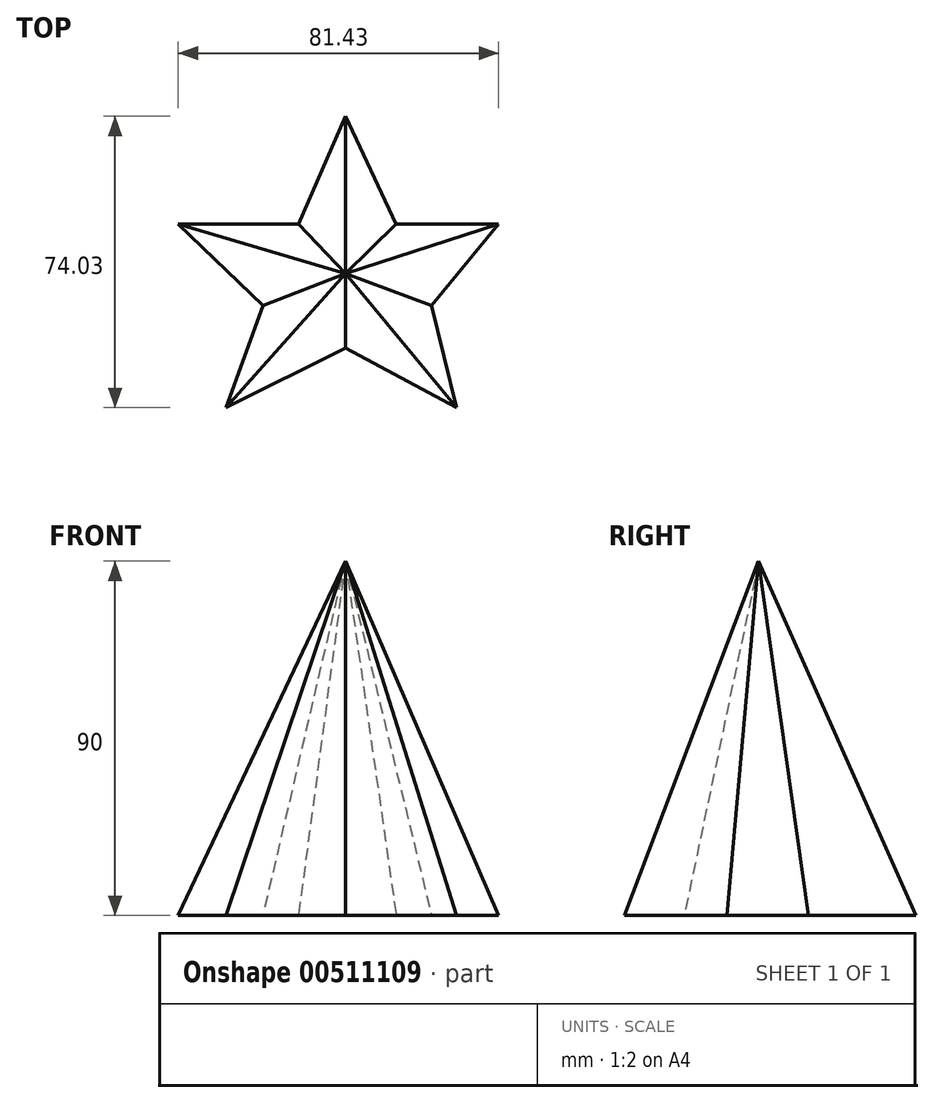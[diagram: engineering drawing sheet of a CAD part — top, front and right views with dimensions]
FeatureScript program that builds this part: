
annotation { "Feature Type Name" : "Feature", "Feature Type Description" : "" }
export const myFeature = defineFeature(function(context is Context, id is Id, definition is map)
    precondition{}
    {
        {
            var Q0;
            Q0=qCreatedBy(makeId("Top.planeOp"),FACE);
            var sketch = newSketch(context, id + "F0", { "sketchPlane" : qUnion([Q0])});
            skLineSegment(sketch, "E0", {"start": v(0, 37.16) * mm, "end": v(-11.95, 9.76) * mm});
            skLineSegment(sketch, "E1", {"start": v(-11.95, 9.76) * mm, "end": v(-42.5, 9.76) * mm});
            skLineSegment(sketch, "E2", {"start": v(-42.5, 9.76) * mm, "end": v(-20.99, -10.93) * mm});
            skLineSegment(sketch, "E3", {"start": v(-20.99, -10.93) * mm, "end": v(-30.39, -36.87) * mm});
            skLineSegment(sketch, "E4", {"start": v(-30.39, -36.87) * mm, "end": v(0, -21.71) * mm});
            skLineSegment(sketch, "E5", {"start": v(0, -21.71) * mm, "end": v(28.27, -36.87) * mm});
            skLineSegment(sketch, "E6", {"start": v(28.27, -36.87) * mm, "end": v(21.86, -10.93) * mm});
            skLineSegment(sketch, "E7", {"start": v(21.86, -10.93) * mm, "end": v(38.93, 9.76) * mm});
            skLineSegment(sketch, "E8", {"start": v(38.93, 9.76) * mm, "end": v(12.87, 9.76) * mm});
            skLineSegment(sketch, "E9", {"start": v(12.87, 9.76) * mm, "end": v(0, 37.16) * mm});
            skSolve(sketch);
        }
        {
            var Q0;
            Q0=qCreatedBy(makeId("Top.planeOp"),FACE);
            cPlane(context, id + "F1", {"entities" : qUnion([Q0]), "cplaneType" : CPlaneType.OFFSET, "offset" : 90 * mm, "width" : 152.4 * mm, "height" : 152.4 * mm});
        }
        {
            var Q0;
            Q0=qCreatedBy(id+"F1.planeOp",FACE);
            var sketch = newSketch(context, id + "F2", { "sketchPlane" : qUnion([Q0])});
            skPoint(sketch, "E10", {"position": v(0, -2.82) * mm});
            skSolve(sketch);
        }
        {
            var Q0;
            Q0=sQuery(id+"F2.wireOp",VERTEX,"E10");
            var Q1;
            Q1=makeQuery(id+"F0.imprint","IMPRINT",FACE,{"disambiguationData":[TD([[makeQuery(id+"F0.imprint","IMPRINT",EDGE,{"derivedFrom":sQuery(id+"F0.wireOp",EDGE,"E0")}),1.0]])]});
            loft(context, id + "F3", {"sheetProfilesArray" : [{ "sheetProfileEntities" : qUnion([Q0]) }, { "sheetProfileEntities" : qUnion([Q1]) }]});
        }
    });
